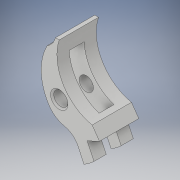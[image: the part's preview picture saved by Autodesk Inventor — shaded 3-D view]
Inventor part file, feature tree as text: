
AUTODESK INVENTOR PART (.ipt)
format: ipt  version: 2018.3 (Build 223284000, 284)  size: 176,640 bytes
history: native  units: in
note: dims shown in document units (in); Inventor stores cm internally (conversion verified against a paired STEP export)
features: extrude x2, sketch x2, chamfer x1
ambient origin geometry x8: Origin, YZ Plane, XZ Plane, XY Plane, X Axis, Y Axis, Z Axis, Center Point
bodies: Solid1 (feature_tree)
feature tree (5):
  extrude  "Extrusion1"  Depth=0.294in
  chamfer  "Chamfer1"  Distance=0.3779in
  extrude  "Extrusion2"  Depth=0.117in
  sketch  "Sketch1"  dims[d0=0.111in d1=0.294in]
  sketch  "Sketch2"  dims[d2=0.346in d3=0.3779in d5=0.186in d6=0.1725in d7=0.249in d8=0.395in d10=0.126in d12=0.03in d13=0.15in d14=0.0115in d15=0.022in d16=0.19in d19=0.284in d20=0.4045in d21=0.4395in d22=0.14in d23=0.03in d24=0.394in d25=0.309in d26=0.0in d27=0.0125in d28=0.125in d29=45.0deg d30=0.1725in d31=1.04in d32=0.032in d33=0.33in d34=0.08in d35=0.117in d36=0.0in]
